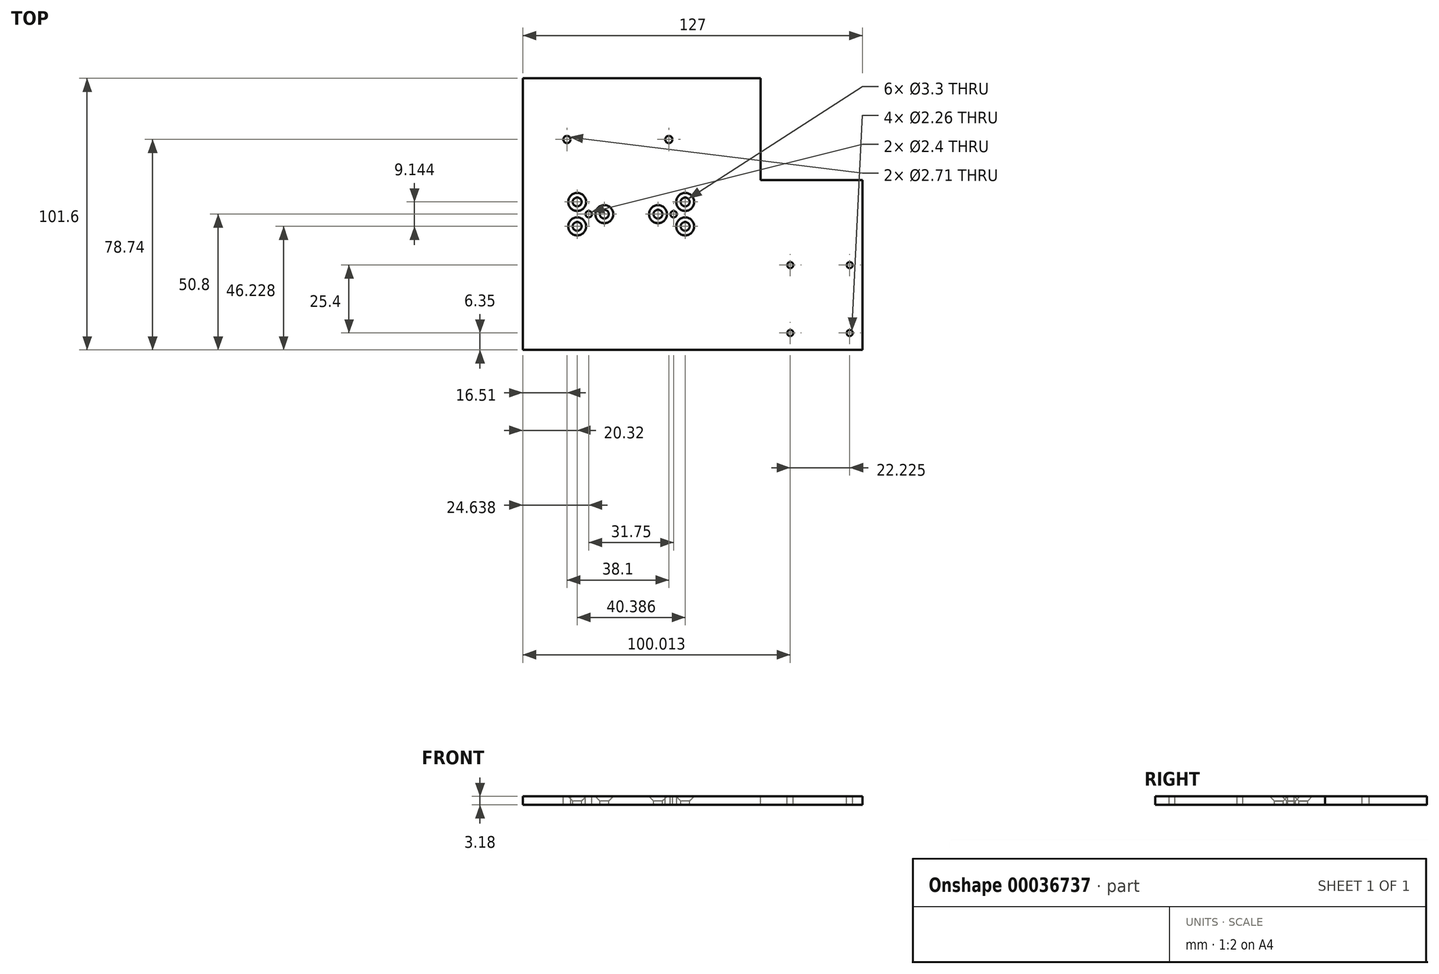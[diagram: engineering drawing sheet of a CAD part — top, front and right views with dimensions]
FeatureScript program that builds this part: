
annotation { "Feature Type Name" : "Feature", "Feature Type Description" : "" }
export const myFeature = defineFeature(function(context is Context, id is Id, definition is map)
    precondition{}
    {
        {
            var Q0;
            Q0=qCreatedBy(makeId("Front.planeOp"),FACE);
            var sketch = newSketch(context, id + "F0", { "sketchPlane" : qUnion([Q0])});
            skLineSegment(sketch, "E0", {"start": v(0, 0) * mm, "end": v(0, 3.18) * mm});
            skLineSegment(sketch, "E1", {"start": v(0, 3.18) * mm, "end": v(-127, 3.17) * mm});
            skLineSegment(sketch, "E2", {"start": v(-127, 3.17) * mm, "end": v(-127, 0) * mm});
            skLineSegment(sketch, "E3", {"start": v(-127, 0) * mm, "end": v(0, 0) * mm});
            skSolve(sketch);
        }
        {
            var Q0;
            Q0=makeQuery(id+"F0.imprint","IMPRINT",FACE,{"disambiguationData":[TD([[makeQuery(id+"F0.imprint","IMPRINT",EDGE,{"derivedFrom":sQuery(id+"F0.wireOp",EDGE,"E0")}),1.0]])]});
            extrude(context, id + "F1", {"entities" : qUnion([Q0]), "endBound" : BoundingType.SYMMETRIC, "depth" : 101.6 * mm, "offsetDistance" : 25.4 * mm});
        }
        {
            var Q0;
            Q0=makeQuery(id+"F1.opExtrude","SWEPT_FACE",FACE,{"disambiguationData":[OSD([sQuery(id+"F0.wireOp",EDGE,"E1")])]});
            var sketch = newSketch(context, id + "F2", { "sketchPlane" : qUnion([Q0])});
            skPoint(sketch, "E4", {"position": v(-106.68, 4.57) * mm});
            skPoint(sketch, "E5", {"position": v(-106.68, -4.57) * mm});
            skPoint(sketch, "E6", {"position": v(-96.52, 0) * mm});
            skPoint(sketch, "E7", {"position": v(-76.45, 0) * mm});
            skPoint(sketch, "E8", {"position": v(-66.3, 4.57) * mm});
            skPoint(sketch, "E9", {"position": v(-66.3, -4.57) * mm});
            skLineSegment(sketch, "E10", {"start": v(-127, 0) * mm, "end": v(-45.97, 0) * mm, "construction": true});
            skLineSegment(sketch, "E11", {"start": v(-86.49, 0) * mm, "end": v(-86.49, 9.55) * mm, "construction": true});
            skSolve(sketch);
        }
        {
            var Q0;
            Q0=sQuery(id+"F2.wireOp",VERTEX,"E8");
            var Q1;
            Q1=sQuery(id+"F2.wireOp",VERTEX,"E9");
            var Q2;
            Q2=sQuery(id+"F2.wireOp",VERTEX,"E7");
            var Q3;
            Q3=sQuery(id+"F2.wireOp",VERTEX,"E6");
            var Q4;
            Q4=sQuery(id+"F2.wireOp",VERTEX,"E4");
            var Q5;
            Q5=sQuery(id+"F2.wireOp",VERTEX,"E5");
            var Q6;
            Q6=makeQuery(id+"F1.opExtrude","SWEPT_BODY",BODY,{"disambiguationData":[OSD([sQuery(id+"F0.wireOp",EDGE,"E0"),sQuery(id+"F0.wireOp",EDGE,"f2e0e0e0-cd28-4836-966f-49551ec3c4cd"),sQuery(id+"F0.wireOp",EDGE,"6f173ce0-8d91-4cf6-bb4e-4d458c8b243f"),sQuery(id+"F0.wireOp",EDGE,"E1"),sQuery(id+"F0.wireOp",EDGE,"E2"),sQuery(id+"F0.wireOp",EDGE,"E3")])]});
            hole(context, id + "F3", {"style" : HoleStyle.C_SINK, "endStyle" : HoleEndStyle.THROUGH, "standardTappedOrClearance" : lookupTablePath({ "standard" : "ISO", "fit" : "Normal", "size" : "M3", "type" : "Clearance" }), "standardBlindInLast" : lookupTablePath({ "fit" : "Standard", "standard" : "ISO", "size" : "M3", "type" : "Clearance" }), "holeDiameter" : 3.3 * mm, "cSinkDiameter" : 6.72 * mm, "cSinkAngle" : 90 * degree, "tappedDepth" : 6.35 * mm, "tapClearance" : 3, "locations" : qUnion([Q0, Q1, Q2, Q3, Q4, Q5]), "scope" : qUnion([Q6])});
        }
        {
            var Q0;
            Q0=makeQuery(id+"F1.opExtrude","SWEPT_FACE",FACE,{"disambiguationData":[OSD([sQuery(id+"F0.wireOp",EDGE,"E1")])]});
            var sketch = newSketch(context, id + "F4", { "sketchPlane" : qUnion([Q0])});
            skPoint(sketch, "E12", {"position": v(-102.36, 0) * mm});
            skPoint(sketch, "E13", {"position": v(-70.61, 0) * mm});
            skLineSegment(sketch, "E14", {"start": v(-96.52, 0) * mm, "end": v(-76.45, 0) * mm, "construction": true});
            skLineSegment(sketch, "E15", {"start": v(-86.49, 0) * mm, "end": v(-86.49, 30.5) * mm, "construction": true});
            skSolve(sketch);
        }
        {
            var Q0;
            Q0=sQuery(id+"F4.wireOp",VERTEX,"E12");
            var Q1;
            Q1=sQuery(id+"F4.wireOp",VERTEX,"E13");
            var Q2;
            Q2=makeQuery(id+"F1.opExtrude","SWEPT_BODY",BODY,{"disambiguationData":[OSD([sQuery(id+"F0.wireOp",EDGE,"E0"),sQuery(id+"F0.wireOp",EDGE,"f2e0e0e0-cd28-4836-966f-49551ec3c4cd"),sQuery(id+"F0.wireOp",EDGE,"6f173ce0-8d91-4cf6-bb4e-4d458c8b243f"),sQuery(id+"F0.wireOp",EDGE,"E1"),sQuery(id+"F0.wireOp",EDGE,"E2"),sQuery(id+"F0.wireOp",EDGE,"E3")])]});
            hole(context, id + "F5", {"style" : HoleStyle.SIMPLE, "endStyle" : HoleEndStyle.THROUGH, "standardTappedOrClearance" : lookupTablePath({ "standard" : "ISO", "engagement" : "75%", "pitch" : "0.6 mm", "size" : "M3", "type" : "Tapped" }), "standardBlindInLast" : lookupTablePath({ "standard" : "ISO", "engagement" : "75%", "pitch" : "0.6 mm", "size" : "M3", "type" : "Tapped" }), "holeDiameter" : 2.4 * mm, "showTappedDepth" : true, "tappedDepth" : 6.35 * mm, "tapClearance" : 3, "locations" : qUnion([Q0, Q1]), "scope" : qUnion([Q2])});
        }
        {
            var Q0;
            Q0=makeQuery(id+"F1.opExtrude","SWEPT_FACE",FACE,{"disambiguationData":[OSD([sQuery(id+"F0.wireOp",EDGE,"E1")])]});
            var sketch = newSketch(context, id + "F6", { "sketchPlane" : qUnion([Q0])});
            skLineSegment(sketch, "E16.bottom", {"start": v(0, 50.8) * mm, "end": v(-38.1, 50.8) * mm});
            skLineSegment(sketch, "E16.top", {"start": v(0, 12.7) * mm, "end": v(-38.1, 12.7) * mm});
            skLineSegment(sketch, "E16.left", {"start": v(0, 50.8) * mm, "end": v(0, 12.7) * mm});
            skLineSegment(sketch, "E16.right", {"start": v(-38.1, 50.8) * mm, "end": v(-38.1, 12.7) * mm});
            skSolve(sketch);
        }
        {
            var Q0;
            Q0=makeQuery(id+"F6.imprint","IMPRINT",FACE,{"disambiguationData":[TD([[makeQuery(id+"F6.imprint","IMPRINT",EDGE,{"derivedFrom":sQuery(id+"F6.wireOp",EDGE,"E16.bottom")}),1.0]])]});
            extrude(context, id + "F7", {"entities" : qUnion([Q0]), "operationType" : NewBodyOperationType.REMOVE, "endBound" : BoundingType.THROUGH_ALL, "oppositeDirection" : true, "depth" : 25.4 * mm, "offsetDistance" : 25.4 * mm});
        }
        {
            var Q0;
            Q0=makeQuery(id+"F1.opExtrude","SWEPT_FACE",FACE,{"disambiguationData":[OSD([sQuery(id+"F0.wireOp",EDGE,"E1")])]});
            var sketch = newSketch(context, id + "F8", { "sketchPlane" : qUnion([Q0])});
            skPoint(sketch, "E17", {"position": v(-4.76, -44.45) * mm});
            skPoint(sketch, "E18", {"position": v(-26.99, -44.45) * mm});
            skPoint(sketch, "E19", {"position": v(-26.99, -19.05) * mm});
            skPoint(sketch, "E20", {"position": v(-4.76, -19.05) * mm});
            skSolve(sketch);
        }
        {
            var Q0;
            Q0=sQuery(id+"F8.wireOp",VERTEX,"E18");
            var Q1;
            Q1=sQuery(id+"F8.wireOp",VERTEX,"E19");
            var Q2;
            Q2=sQuery(id+"F8.wireOp",VERTEX,"E20");
            var Q3;
            Q3=sQuery(id+"F8.wireOp",VERTEX,"E17");
            var Q4;
            Q4=makeQuery(id+"F1.opExtrude","SWEPT_BODY",BODY,{"disambiguationData":[OSD([sQuery(id+"F0.wireOp",EDGE,"E0"),sQuery(id+"F0.wireOp",EDGE,"E1"),sQuery(id+"F0.wireOp",EDGE,"E2"),sQuery(id+"F0.wireOp",EDGE,"E3")])]});
            hole(context, id + "F9", {"style" : HoleStyle.SIMPLE, "endStyle" : HoleEndStyle.THROUGH, "standardTappedOrClearance" : lookupTablePath({ "standard" : "ANSI", "engagement" : "75%", "pitch" : "40 tpi", "size" : "#4", "type" : "Tapped" }), "standardBlindInLast" : lookupTablePath({ "standard" : "ANSI", "engagement" : "75%", "pitch" : "40 tpi", "size" : "#4", "type" : "Tapped" }), "holeDiameter" : 2.26 * mm, "majorDiameter" : 2.84 * mm, "showTappedDepth" : true, "tappedDepth" : 6.35 * mm, "tapClearance" : 3, "locations" : qUnion([Q0, Q1, Q2, Q3]), "scope" : qUnion([Q4])});
        }
        {
            var Q0;
            Q0=makeQuery(id+"F1.opExtrude","SWEPT_FACE",FACE,{"disambiguationData":[OSD([sQuery(id+"F0.wireOp",EDGE,"E1")])]});
            var sketch = newSketch(context, id + "F10", { "sketchPlane" : qUnion([Q0])});
            skPoint(sketch, "E21", {"position": v(-110.5, 27.94) * mm});
            skPoint(sketch, "E22", {"position": v(-72.4, 27.94) * mm});
            skSolve(sketch);
        }
        {
            var Q0;
            Q0=sQuery(id+"F10.wireOp",VERTEX,"E21");
            var Q1;
            Q1=sQuery(id+"F10.wireOp",VERTEX,"E22");
            var Q2;
            Q2=makeQuery(id+"F1.opExtrude","SWEPT_BODY",BODY,{"disambiguationData":[OSD([sQuery(id+"F0.wireOp",EDGE,"E0"),sQuery(id+"F0.wireOp",EDGE,"E1"),sQuery(id+"F0.wireOp",EDGE,"E2"),sQuery(id+"F0.wireOp",EDGE,"E3")])]});
            hole(context, id + "F11", {"style" : HoleStyle.SIMPLE, "endStyle" : HoleEndStyle.THROUGH, "standardTappedOrClearance" : lookupTablePath({ "standard" : "ANSI", "engagement" : "75%", "pitch" : "32 tpi", "size" : "#6", "type" : "Tapped" }), "standardBlindInLast" : lookupTablePath({ "standard" : "ANSI", "engagement" : "75%", "pitch" : "32 tpi", "size" : "#6", "type" : "Tapped" }), "holeDiameter" : 2.7 * mm, "majorDiameter" : 3.5 * mm, "showTappedDepth" : true, "tappedDepth" : 6.35 * mm, "tapClearance" : 3, "locations" : qUnion([Q0, Q1]), "scope" : qUnion([Q2])});
        }
    });
